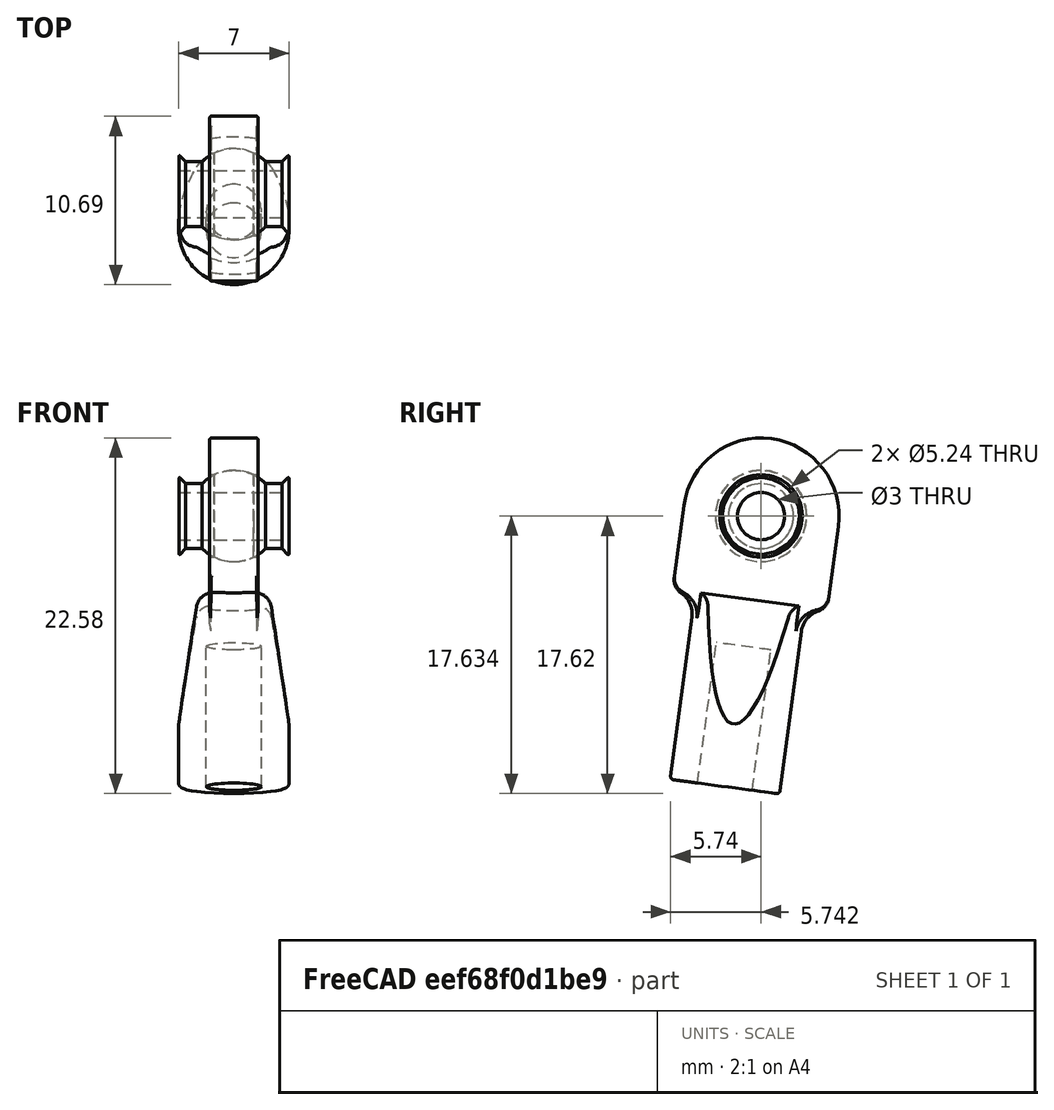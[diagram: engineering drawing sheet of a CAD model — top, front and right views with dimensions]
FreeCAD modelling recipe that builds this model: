
FCSTD DOCUMENT  (FreeCAD 2022.430R26244 +4758 (Git))
Label: As3Traxxas5347BallJoint
License: All rights reserved
LicenseURL: http://en.wikipedia.org/wiki/All_rights_reserved
objects: Part::FeaturePython×13, App::FeaturePython×4, Part::Feature×2, Part::SubShapeBinder×1, PartDesign::Plane×1
note: 15 computed .brp shape members not serialized (recipe doc carries the construction recipe); baked Part::Feature solids carry a one-line shape summary decoded from their .brp

FEATURE [Part::Feature] Solid  label="5347 ball"
  TreeRank = 11
  shape: bbox 6.98 x 5.77 x 5.77 mm, 10 faces (baked)
FEATURE [Part::Feature] Solid001  label="rod end 5347"
  Placement = pos=(-0.00421036,0.0017498,0.0142902) rot=(0.550048,0.628407,0.550048;2.0195rad)
  TreeRank = 12
  shape: bbox 7.577 x 11.49 x 22.98 mm, 43 faces (baked)
FEATURE [App::FeaturePython] Constraints  # WARN: FeaturePython — macro-defined, semantics opaque (R4)
  TreeRank = 8
  _LinkVersion = 1
  _Version = 1
FEATURE [Part::FeaturePython] Parts  # WARN: FeaturePython — macro-defined, semantics opaque (R4)
  Group = -> [Solid]
  GroupMode = 0
  TreeRank = 10
  _LinkVersion = 1
FEATURE [App::FeaturePython] Constraints001  # WARN: FeaturePython — macro-defined, semantics opaque (R4)
  TreeRank = 16
  _LinkVersion = 1
  _Version = 1
FEATURE [Part::SubShapeBinder] Import  label="Import(rod end 5347)"
  BindCopyOnChange = 0
  BindMode = 0
  ClaimChildren = false
  FillStyle = 0
  Fuse = false
  MakeFace = false
  PartialLoad = false
  Relative = true
  Support = -> [Solid001]
  TreeRank = 27
  _Version = 8
FEATURE [PartDesign::Plane] DatumPlane
  AttachmentOffset = pos=(0,0,0) rot=(1,0,0;1.5708rad)
  Length = 10
  MapMode = 5
  MinimumLength = 10
  MinimumWidth = 10
  Placement = pos=(0,-2.29526,-17.183) rot=(1,0,0;4.5796rad)
  ResizeMode = 0
  Support = -> [Import]
  TreeRank = 26
  Width = 24.8985
FEATURE [Part::FeaturePython] Parts001  # WARN: FeaturePython — macro-defined, semantics opaque (R4)
  Group = -> [Solid001,DatumPlane,Import]
  GroupMode = 0
  TreeRank = 18
  _LinkVersion = 1
FEATURE [Part::FeaturePython] Assembly  label="As3Traxxas5347ball"  # WARN: FeaturePython — macro-defined, semantics opaque (R4)
  AutoRelax = true
  BuildShape = 0
  Freeze = false
  Group = -> [Constraints,Elements,Parts]
  TreeRank = 7
  Verbose = false
  _LinkVersion = 1
  _SolverType = 1
  _Version = 1
FEATURE [App::FeaturePython] Elements  # WARN: FeaturePython — macro-defined, semantics opaque (R4)
  Group = -> [Element001,Element003,Element007]
  TreeRank = 9
  _LinkVersion = 1
FEATURE [Part::FeaturePython] Element001  label="ElSphereM"  # link proxy (typed FeaturePython)
  Detach = false
  LinkTransform = true
  LinkedObject = -> Solid [Face8]
  TreeRank = 14
  _LinkVersion = 1
  _Parent = -> Elements
FEATURE [Part::FeaturePython] Assembly001  label="As3rodEnd5347"  # WARN: FeaturePython — macro-defined, semantics opaque (R4)
  AutoRelax = true
  BuildShape = 0
  Freeze = false
  Group = -> [Constraints001,Elements001,Parts001]
  TreeRank = 15
  Verbose = false
  _LinkVersion = 1
  _SolverType = 1
  _Version = 1
FEATURE [App::FeaturePython] Elements001  # WARN: FeaturePython — macro-defined, semantics opaque (R4)
  Group = -> [Element,Element002,Element004,Element005,Element006,Element008]
  TreeRank = 17
  _LinkVersion = 1
FEATURE [Part::FeaturePython] Element  label="ElSphereF"  # link proxy (typed FeaturePython)
  Detach = false
  LinkTransform = true
  LinkedObject = -> Solid001 [Face1]
  TreeRank = 19
  _LinkVersion = 1
  _Parent = -> Elements001
FEATURE [Part::FeaturePython] Element002  label="ElCircle1"  # link proxy (typed FeaturePython)
  Detach = false
  LinkTransform = true
  LinkedObject = -> Solid001 [Edge8]
  TreeRank = 20
  _LinkVersion = 1
  _Parent = -> Elements001
FEATURE [Part::FeaturePython] Element003  label="ElCircle"  # link proxy (typed FeaturePython)
  Detach = false
  LinkTransform = true
  LinkedObject = -> Solid [Edge10]
  TreeRank = 21
  _LinkVersion = 1
  _Parent = -> Elements
FEATURE [Part::FeaturePython] Element004  label="ElCircle2"  # link proxy (typed FeaturePython)
  Detach = false
  LinkTransform = true
  LinkedObject = -> Solid001 [Edge6]
  TreeRank = 22
  _LinkVersion = 1
  _Parent = -> Elements001
FEATURE [Part::FeaturePython] Element005  label="ElPlane"  # link proxy (typed FeaturePython)
  Detach = false
  LinkTransform = true
  LinkedObject = -> Solid001 [Face42]
  TreeRank = 23
  _LinkVersion = 1
  _Parent = -> Elements001
FEATURE [Part::FeaturePython] Element006  # link proxy (typed FeaturePython)
  Detach = false
  LinkTransform = true
  LinkedObject = -> Solid001 [Face32]
  TreeRank = 24
  _LinkVersion = 1
  _Parent = -> Elements001
FEATURE [Part::FeaturePython] Element007  # link proxy (typed FeaturePython)
  Detach = false
  LinkTransform = true
  LinkedObject = -> Solid [Face3]
  TreeRank = 25
  _LinkVersion = 1
  _Parent = -> Elements
FEATURE [Part::FeaturePython] Element008  label="ElSymSphF"  # link proxy (typed FeaturePython)
  Detach = false
  LinkTransform = true
  LinkedObject = -> DatumPlane
  TreeRank = 28
  _LinkVersion = 1
  _Parent = -> Elements001
